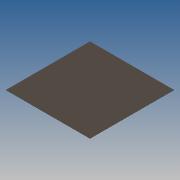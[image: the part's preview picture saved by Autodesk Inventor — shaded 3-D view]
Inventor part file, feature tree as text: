
AUTODESK INVENTOR PART (.ipt)
format: ipt  version: 2014 SP1 (Build 180222100, 222)  size: 74,752 bytes
history: native  units: in
note: dims shown in document units (in); Inventor stores cm internally (conversion verified against a paired STEP export)
features: extrude x1, sketch x1
ambient origin geometry x8: Origin, YZ Plane, XZ Plane, XY Plane, X Axis, Y Axis, Z Axis, Center Point
bodies: Solid1 (feature_tree)
feature tree (2):
  extrude  "Extrusion1"  Depth=1200.0in
  sketch  "Sketch1"  dims[d0=1200.0in d1=1200.0in d2=2.0in d3=0.0in]
